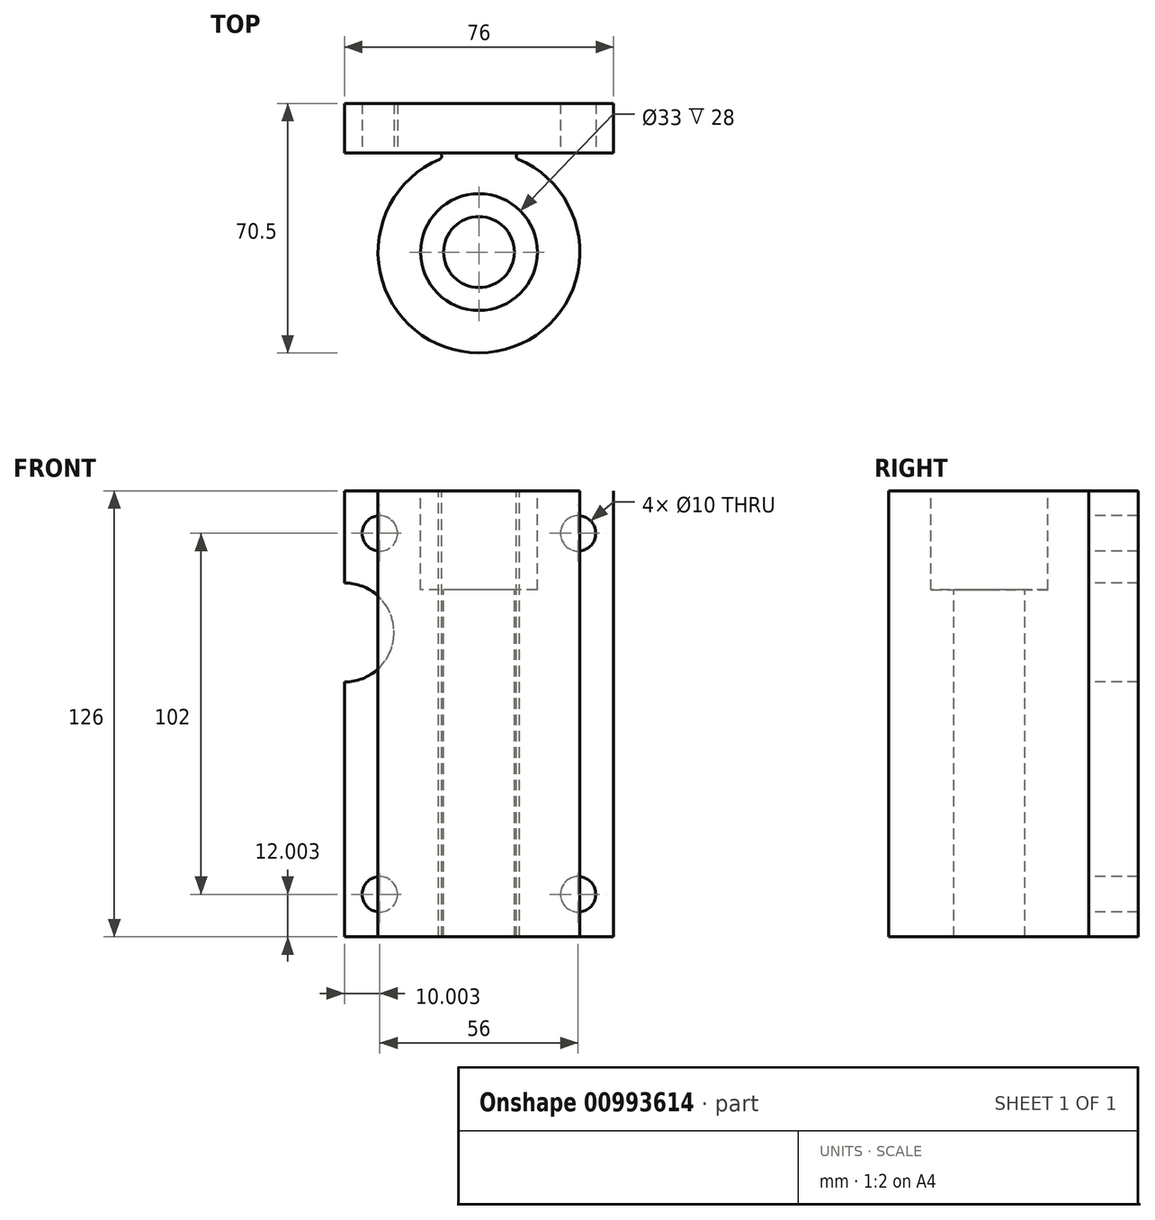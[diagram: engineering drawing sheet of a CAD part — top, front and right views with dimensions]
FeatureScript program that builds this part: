
annotation { "Feature Type Name" : "Feature", "Feature Type Description" : "" }
export const myFeature = defineFeature(function(context is Context, id is Id, definition is map)
    precondition{}
    {
        {
            var Q0;
            Q0=qCreatedBy(makeId("Front.planeOp"),FACE);
            var sketch = newSketch(context, id + "F0", { "sketchPlane" : qUnion([Q0])});
            skLineSegment(sketch, "E0.bottom", {"start": v(-50.48, 54.5) * mm, "end": v(25.52, 54.5) * mm});
            skLineSegment(sketch, "E0.top", {"start": v(-50.48, -71.5) * mm, "end": v(25.52, -71.5) * mm});
            skLineSegment(sketch, "E0.left", {"start": v(-50.48, 54.5) * mm, "end": v(-50.48, 28.5) * mm});
            skLineSegment(sketch, "E0.right", {"start": v(25.52, 54.5) * mm, "end": v(25.52, -71.5) * mm});
            skCircle(sketch, "E1", {"center": v(-40.48, 42.5) * mm, "radius": 5 * mm});
            skCircle(sketch, "E2", {"center": v(15.52, 42.5) * mm, "radius": 5 * mm});
            skCircle(sketch, "E3", {"center": v(-40.48, -59.5) * mm, "radius": 5 * mm});
            skCircle(sketch, "E4", {"center": v(15.52, -59.5) * mm, "radius": 5 * mm});
            skArc(sketch, "E5", {"start": v(-50.48, 0.5) * mm, "mid": v(-36.48, 14.5) * mm, "end": v(-50.48, 28.5) * mm});
            skLineSegment(sketch, "E6.trimOffspring", {"start": v(-50.48, 0.5) * mm, "end": v(-50.48, -71.5) * mm});
            skSolve(sketch);
        }
        {
            var Q0;
            Q0=makeQuery(id+"F0.imprint","IMPRINT",FACE,{"disambiguationData":[TD([[makeQuery(id+"F0.imprint","IMPRINT",EDGE,{"derivedFrom":sQuery(id+"F0.wireOp",EDGE,"E0.bottom")}),-1.0]])]});
            extrude(context, id + "F1", {"entities" : qUnion([Q0]), "oppositeDirection" : true, "depth" : 19 * mm, "offsetDistance" : 25 * mm});
        }
        {
            var Q0;
            Q0=makeQuery(id+"F1.opExtrude","SWEPT_FACE",FACE,{"disambiguationData":[OSD([sQuery(id+"F0.wireOp",EDGE,"E0.top")])]});
            var sketch = newSketch(context, id + "F2", { "sketchPlane" : qUnion([Q0])});
            skLineSegment(sketch, "E7.bottom", {"start": v(-50.48, 0) * mm, "end": v(25.52, 0) * mm});
            skLineSegment(sketch, "E7.top", {"start": v(-50.48, -5) * mm, "end": v(25.52, -5) * mm});
            skLineSegment(sketch, "E7.left", {"start": v(-50.48, 0) * mm, "end": v(-50.48, -5) * mm});
            skLineSegment(sketch, "E7.right", {"start": v(25.52, 0) * mm, "end": v(25.52, -5) * mm});
            skSolve(sketch);
        }
        {
            var Q0;
            Q0=makeQuery(id+"F2.imprint","IMPRINT",FACE,{"disambiguationData":[TD([[makeQuery(id+"F2.imprint","IMPRINT",EDGE,{"derivedFrom":sQuery(id+"F2.wireOp",EDGE,"E7.bottom")}),-1.0]])]});
            extrude(context, id + "F3", {"entities" : qUnion([Q0]), "operationType" : NewBodyOperationType.REMOVE, "endBound" : BoundingType.THROUGH_ALL, "oppositeDirection" : true, "depth" : 25 * mm, "offsetDistance" : 25 * mm});
        }
        {
            var Q0;
            Q0=makeQuery(id+"F1.opExtrude","SWEPT_FACE",FACE,{"disambiguationData":[OSD([sQuery(id+"F0.wireOp",EDGE,"E0.bottom")])]});
            var sketch = newSketch(context, id + "F4", { "sketchPlane" : qUnion([Q0])});
            skArc(sketch, "E8", {"start": v(-23.53, 3.27) * mm, "mid": v(-12.48, -51.5) * mm, "end": v(-1.42, 3.27) * mm});
            skCircle(sketch, "E9", {"center": v(-12.48, -23) * mm, "radius": 10 * mm});
            skPoint(sketch, "E10.visualSharp", {"position": v(-17.8, 5) * mm});
            skArc(sketch, "E10.filletArc", {"start": v(-23.53, 3.27) * mm, "mid": v(-23, 4.28) * mm, "end": v(-23.88, 5) * mm});
            skPoint(sketch, "E11.visualSharp", {"position": v(-7.16, 5) * mm});
            skArc(sketch, "E11.filletArc", {"start": v(-1.07, 5) * mm, "mid": v(-1.96, 4.28) * mm, "end": v(-1.42, 3.27) * mm});
            skLineSegment(sketch, "E12", {"start": v(-23.88, 5) * mm, "end": v(-1.07, 5) * mm});
            skSolve(sketch);
        }
        {
            var Q0;
            Q0=makeQuery(id+"F4.imprint","IMPRINT",FACE,{"disambiguationData":[TD([[makeQuery(id+"F4.imprint","IMPRINT",EDGE,{"derivedFrom":sQuery(id+"F4.wireOp",EDGE,"E9")}),-1.0]])]});
            var Q1;
            Q1=makeQuery(id+"F1.opExtrude","SWEPT_FACE",FACE,{"disambiguationData":[OSD([sQuery(id+"F0.wireOp",EDGE,"E0.top")])]});
            extrude(context, id + "F5", {"entities" : qUnion([Q0]), "endBound" : BoundingType.UP_TO_SURFACE, "oppositeDirection" : true, "depth" : 25 * mm, "endBoundEntityFace" : qUnion([Q1]), "offsetDistance" : 25 * mm});
        }
        {
            var Q0;
            Q0=makeQuery(id+"F5.opExtrude","CAP_FACE",FACE,{"disambiguationData":[OSD([sQuery(id+"F4.wireOp",EDGE,"E8"),sQuery(id+"F4.wireOp",EDGE,"E9")])],"isStart":true});
            var sketch = newSketch(context, id + "F6", { "sketchPlane" : qUnion([Q0])});
            skCircle(sketch, "E13", {"center": v(-12.48, -23) * mm, "radius": 16.5 * mm});
            skSolve(sketch);
        }
        {
            var Q0;
            Q0 = qSketchRegion(id + "F6", true);
            extrude(context, id + "F7", {"entities" : qUnion([Q0]), "operationType" : NewBodyOperationType.REMOVE, "oppositeDirection" : true, "depth" : 28 * mm, "offsetDistance" : 25 * mm});
        }
    });
